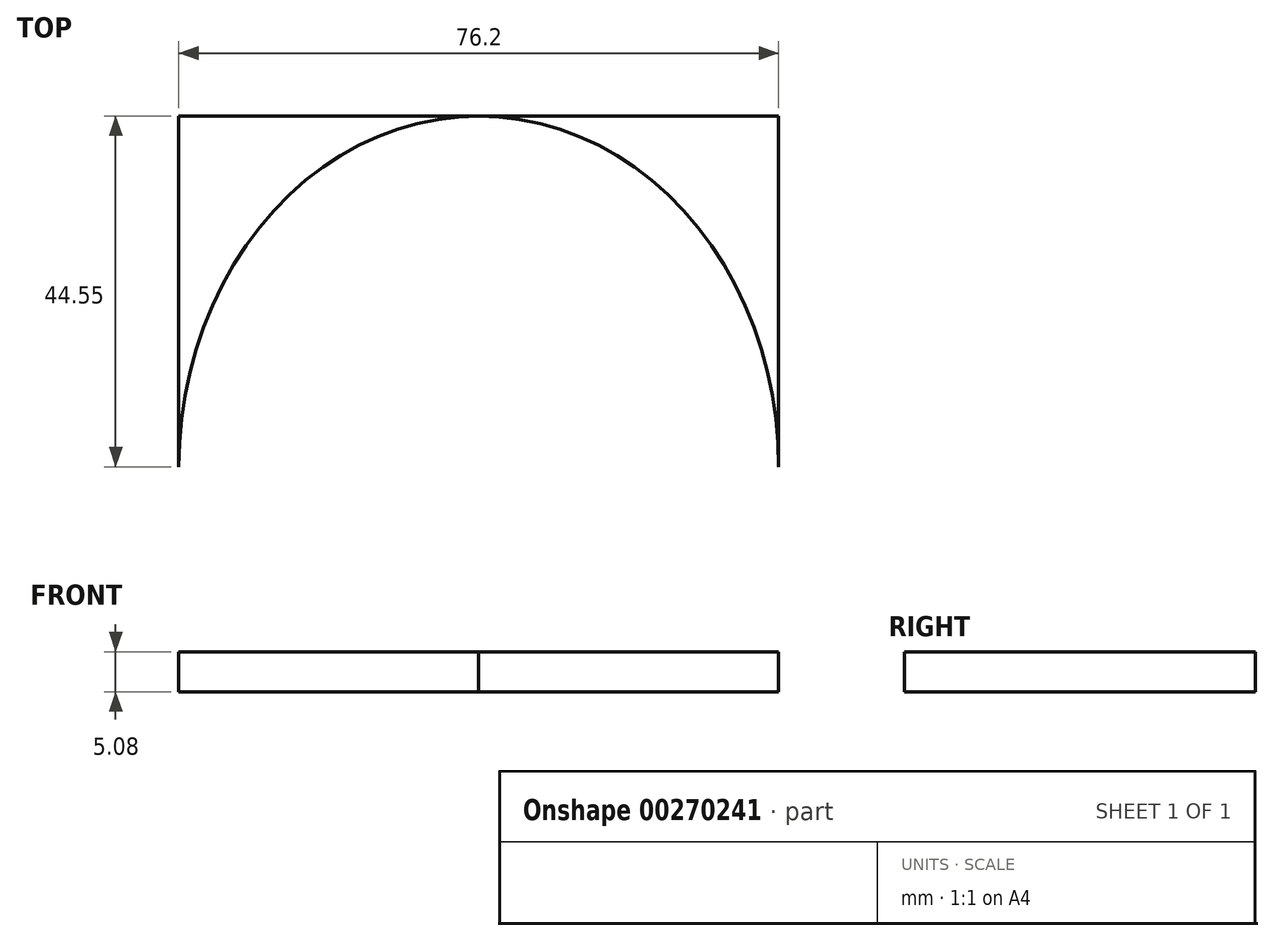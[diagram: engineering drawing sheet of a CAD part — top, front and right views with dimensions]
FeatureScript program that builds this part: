
annotation { "Feature Type Name" : "Feature", "Feature Type Description" : "" }
export const myFeature = defineFeature(function(context is Context, id is Id, definition is map)
    precondition{}
    {
        {
            var Q0;
            Q0=qCreatedBy(makeId("Top.planeOp"),FACE);
            var sketch = newSketch(context, id + "F0", { "sketchPlane" : qUnion([Q0])});
            skLineSegment(sketch, "E0", {"start": v(0, 0) * mm, "end": v(0, 44.55) * mm});
            skLineSegment(sketch, "E1", {"start": v(0, 44.55) * mm, "end": v(0, 0) * mm});
            skLineSegment(sketch, "E2", {"start": v(0, 0) * mm, "end": v(-38.1, 0) * mm});
            skLineSegment(sketch, "E3", {"start": v(-38.1, 0) * mm, "end": v(0, 0) * mm});
            skEllipse(sketch, "E4", {"center": v(0, 0) * mm, "majorRadius": 31.5 * mm, "minorRadius": 23.53 * mm, "majorAxis": v(0, 1)});
            skLineSegment(sketch, "E5", {"start": v(0, 31.5) * mm, "end": v(0, 37.85) * mm});
            skLineSegment(sketch, "E6", {"start": v(-23.53, 0) * mm, "end": v(-29.88, 0) * mm});
            skEllipse(sketch, "E7", {"center": v(0, 0) * mm, "majorRadius": 44.55 * mm, "minorRadius": 38.1 * mm, "majorAxis": v(0, 1)});
            skLineSegment(sketch, "E8", {"start": v(-38.1, 0) * mm, "end": v(-38.1, 44.55) * mm});
            skLineSegment(sketch, "E9", {"start": v(-38.1, 44.55) * mm, "end": v(0, 44.55) * mm});
            skLineSegment(sketch, "E10", {"start": v(38.1, 0) * mm, "end": v(38.1, 44.55) * mm});
            skLineSegment(sketch, "E11", {"start": v(38.1, 44.55) * mm, "end": v(0, 44.55) * mm});
            skSolve(sketch);
        }
        {
            var Q0;
            {var subQ2=sQuery(id+"F0.wireOp",EDGE,"E8");Q0=makeQuery(id+"F0.imprint","IMPRINT",FACE,{"disambiguationData":[TD([[makeQuery(id+"F0.imprint","IMPRINT",EDGE,{"derivedFrom":subQ2}),-1.0]])]});}
            var Q1;
            {var subQ0=sQuery(id+"F0.wireOp",EDGE,"E5");Q1=makeQuery(id+"F0.imprint","IMPRINT",FACE,{"disambiguationData":[TD([[makeQuery(id+"F0.imprint","IMPRINT",EDGE,{"derivedFrom":subQ0}),1.0]])]});}
            var Q2;
            {var subQ0=sQuery(id+"F0.wireOp",EDGE,"E5");Q2=makeQuery(id+"F0.imprint","IMPRINT",FACE,{"disambiguationData":[TD([[makeQuery(id+"F0.imprint","IMPRINT",EDGE,{"derivedFrom":subQ0}),-1.0]])]});}
            var Q3;
            {var subQ2=sQuery(id+"F0.wireOp",EDGE,"E10");Q3=makeQuery(id+"F0.imprint","IMPRINT",FACE,{"disambiguationData":[TD([[makeQuery(id+"F0.imprint","IMPRINT",EDGE,{"derivedFrom":subQ2}),1.0]])]});}
            extrude(context, id + "F1", {"entities" : qUnion([Q0, Q1, Q2, Q3]), "depth" : 5.08 * mm});
        }
    });
